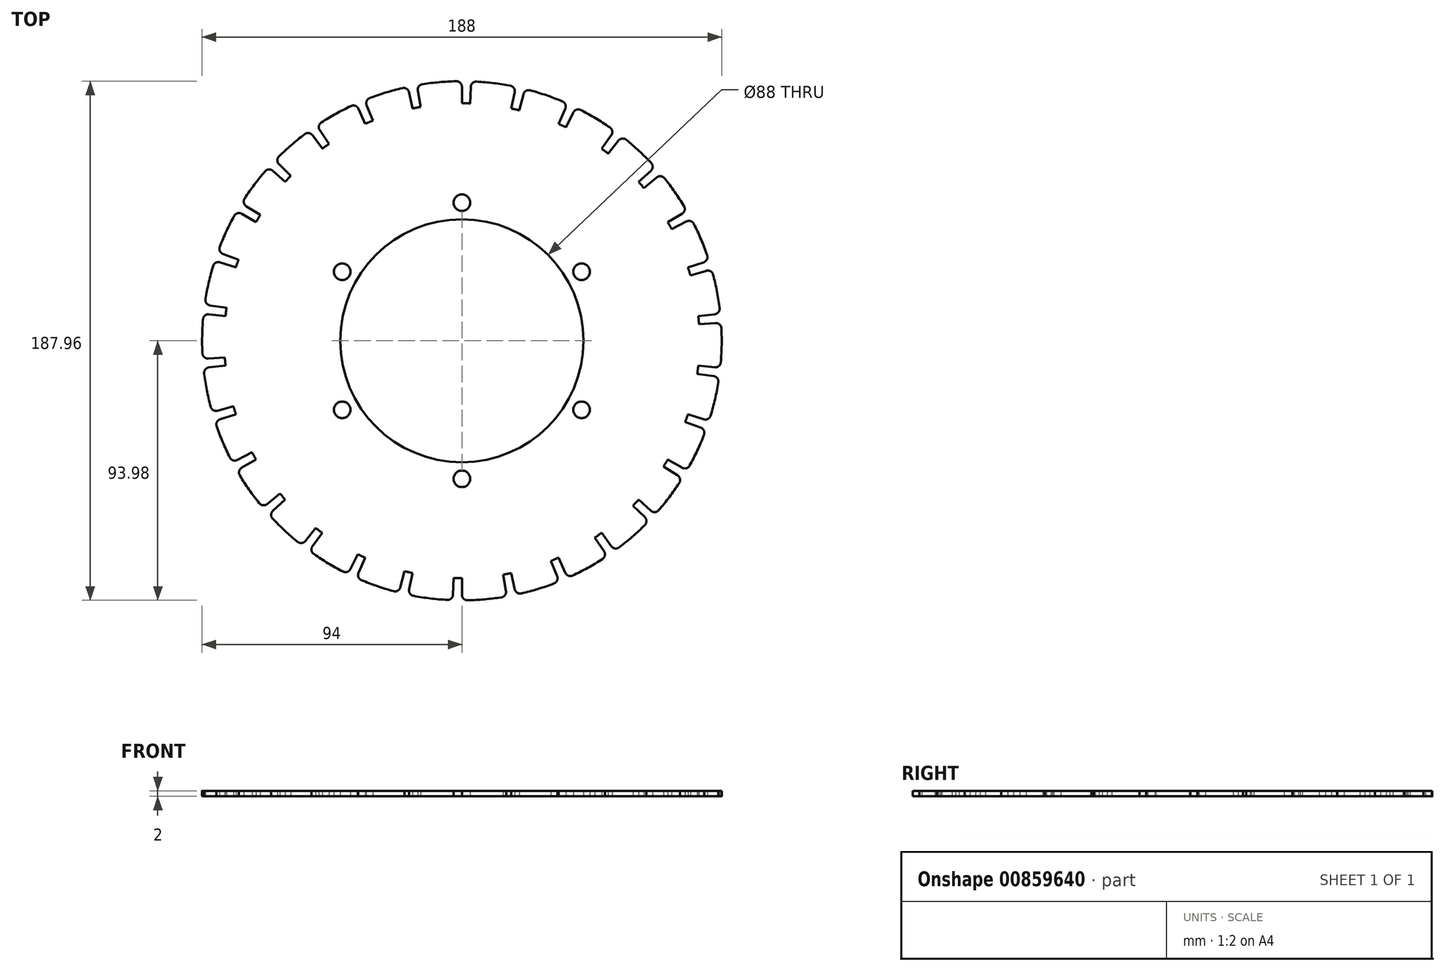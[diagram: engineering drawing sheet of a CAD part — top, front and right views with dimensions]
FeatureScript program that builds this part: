
annotation { "Feature Type Name" : "Feature", "Feature Type Description" : "" }
export const myFeature = defineFeature(function(context is Context, id is Id, definition is map)
    precondition{}
    {
        {
            var Q0;
            Q0=qCreatedBy(makeId("Top.planeOp"),FACE);
            var sketch = newSketch(context, id + "F0", { "sketchPlane" : qUnion([Q0])});
            skCircle(sketch, "E0", {"center": v(0, 0) * mm, "radius": 94 * mm});
            skCircle(sketch, "E1", {"center": v(0, 0) * mm, "radius": 44 * mm});
            skCircle(sketch, "E2", {"center": v(0, 50) * mm, "radius": 3 * mm});
            skCircle(sketch, "E3.1.0", {"center": v(-43.3, 25) * mm, "radius": 3 * mm});
            skCircle(sketch, "E3.2.0", {"center": v(-43.3, -25) * mm, "radius": 3 * mm});
            skCircle(sketch, "E3.3.0", {"center": v(0, -50) * mm, "radius": 3 * mm});
            skCircle(sketch, "E3.4.0", {"center": v(43.3, -25) * mm, "radius": 3 * mm});
            skCircle(sketch, "E3.5.0", {"center": v(43.3, 25) * mm, "radius": 3 * mm});
            skArc(sketch, "E4", {"start": v(0, 86) * mm, "mid": v(1.5, 85.99) * mm, "end": v(3, 85.95) * mm});
            skLineSegment(sketch, "E5", {"start": v(0, 94) * mm, "end": v(0, 86) * mm});
            skLineSegment(sketch, "E6", {"start": v(3.28, 93.94) * mm, "end": v(3, 85.95) * mm});
            skLineSegment(sketch, "E7", {"start": v(0, 0) * mm, "end": v(0, 86) * mm, "construction": true});
            skLineSegment(sketch, "E8", {"start": v(0, 0) * mm, "end": v(3, 85.95) * mm, "construction": true});
            skLineSegment(sketch, "E9.1.0", {"start": v(-16.32, 92.57) * mm, "end": v(-14.93, 84.7) * mm});
            skArc(sketch, "E9.1.1", {"start": v(-17.88, 84.12) * mm, "mid": v(-16.4, 84.42) * mm, "end": v(-14.93, 84.7) * mm});
            skLineSegment(sketch, "E9.1.2", {"start": v(-19.54, 91.95) * mm, "end": v(-17.88, 84.12) * mm});
            skLineSegment(sketch, "E9.2.0", {"start": v(-35.21, 87.16) * mm, "end": v(-32.22, 79.74) * mm});
            skArc(sketch, "E9.2.1", {"start": v(-34.98, 78.56) * mm, "mid": v(-33.6, 79.16) * mm, "end": v(-32.22, 79.74) * mm});
            skLineSegment(sketch, "E9.2.2", {"start": v(-38.23, 85.87) * mm, "end": v(-34.98, 78.56) * mm});
            skLineSegment(sketch, "E9.3.0", {"start": v(-52.56, 77.93) * mm, "end": v(-48.1, 71.3) * mm});
            skArc(sketch, "E9.3.1", {"start": v(-50.55, 69.58) * mm, "mid": v(-49.33, 70.45) * mm, "end": v(-48.1, 71.3) * mm});
            skLineSegment(sketch, "E9.3.2", {"start": v(-55.25, 76.05) * mm, "end": v(-50.55, 69.58) * mm});
            skLineSegment(sketch, "E9.4.0", {"start": v(-67.62, 65.3) * mm, "end": v(-61.86, 59.74) * mm});
            skArc(sketch, "E9.4.1", {"start": v(-63.91, 57.55) * mm, "mid": v(-62.9, 58.65) * mm, "end": v(-61.86, 59.74) * mm});
            skLineSegment(sketch, "E9.4.2", {"start": v(-69.86, 62.9) * mm, "end": v(-63.91, 57.55) * mm});
            skLineSegment(sketch, "E9.5.0", {"start": v(-79.72, 49.81) * mm, "end": v(-72.93, 45.57) * mm});
            skArc(sketch, "E9.5.1", {"start": v(-74.48, 43) * mm, "mid": v(-73.72, 44.3) * mm, "end": v(-72.93, 45.57) * mm});
            skLineSegment(sketch, "E9.5.2", {"start": v(-81.4, 47) * mm, "end": v(-74.48, 43) * mm});
            skLineSegment(sketch, "E9.6.0", {"start": v(-88.33, 32.15) * mm, "end": v(-80.81, 29.41) * mm});
            skArc(sketch, "E9.6.1", {"start": v(-81.8, 26.58) * mm, "mid": v(-81.31, 28) * mm, "end": v(-80.81, 29.41) * mm});
            skLineSegment(sketch, "E9.6.2", {"start": v(-89.4, 29.05) * mm, "end": v(-81.8, 26.58) * mm});
            skLineSegment(sketch, "E9.7.0", {"start": v(-93.09, 13.08) * mm, "end": v(-85.16, 11.97) * mm});
            skArc(sketch, "E9.7.1", {"start": v(-85.53, 8.99) * mm, "mid": v(-85.36, 10.48) * mm, "end": v(-85.16, 11.97) * mm});
            skLineSegment(sketch, "E9.7.2", {"start": v(-93.49, 9.83) * mm, "end": v(-85.53, 8.99) * mm});
            skLineSegment(sketch, "E9.8.0", {"start": v(-93.77, -6.56) * mm, "end": v(-85.8, -6) * mm});
            skArc(sketch, "E9.8.1", {"start": v(-85.53, -8.99) * mm, "mid": v(-85.67, -7.5) * mm, "end": v(-85.8, -6) * mm});
            skLineSegment(sketch, "E9.8.2", {"start": v(-93.49, -9.83) * mm, "end": v(-85.53, -8.99) * mm});
            skLineSegment(sketch, "E9.9.0", {"start": v(-90.36, -25.9) * mm, "end": v(-82.67, -23.7) * mm});
            skArc(sketch, "E9.9.1", {"start": v(-81.8, -26.58) * mm, "mid": v(-82.24, -25.14) * mm, "end": v(-82.67, -23.7) * mm});
            skLineSegment(sketch, "E9.9.2", {"start": v(-89.4, -29.05) * mm, "end": v(-81.8, -26.58) * mm});
            skLineSegment(sketch, "E9.10.0", {"start": v(-83, -44.13) * mm, "end": v(-75.93, -40.37) * mm});
            skArc(sketch, "E9.10.1", {"start": v(-74.48, -43) * mm, "mid": v(-75.22, -41.7) * mm, "end": v(-75.93, -40.37) * mm});
            skLineSegment(sketch, "E9.10.2", {"start": v(-81.4, -47) * mm, "end": v(-74.48, -43) * mm});
            skLineSegment(sketch, "E9.11.0", {"start": v(-72, -60.42) * mm, "end": v(-65.88, -55.28) * mm});
            skArc(sketch, "E9.11.1", {"start": v(-63.91, -57.55) * mm, "mid": v(-64.9, -56.42) * mm, "end": v(-65.88, -55.28) * mm});
            skLineSegment(sketch, "E9.11.2", {"start": v(-69.86, -62.9) * mm, "end": v(-63.91, -57.55) * mm});
            skLineSegment(sketch, "E9.12.0", {"start": v(-57.87, -74.07) * mm, "end": v(-52.95, -67.77) * mm});
            skArc(sketch, "E9.12.1", {"start": v(-50.55, -69.58) * mm, "mid": v(-51.76, -68.68) * mm, "end": v(-52.95, -67.77) * mm});
            skLineSegment(sketch, "E9.12.2", {"start": v(-55.25, -76.05) * mm, "end": v(-50.55, -69.58) * mm});
            skLineSegment(sketch, "E9.13.0", {"start": v(-41.2, -84.49) * mm, "end": v(-37.7, -77.3) * mm});
            skArc(sketch, "E9.13.1", {"start": v(-34.98, -78.56) * mm, "mid": v(-36.35, -77.94) * mm, "end": v(-37.7, -77.3) * mm});
            skLineSegment(sketch, "E9.13.2", {"start": v(-38.23, -85.87) * mm, "end": v(-34.98, -78.56) * mm});
            skLineSegment(sketch, "E9.14.0", {"start": v(-20.8, -83.45) * mm, "end": v(-22.74, -91.2) * mm});
            skArc(sketch, "E9.14.1", {"start": v(-17.88, -84.12) * mm, "mid": v(-19.35, -83.8) * mm, "end": v(-20.8, -83.45) * mm});
            skLineSegment(sketch, "E9.14.2", {"start": v(-19.54, -91.95) * mm, "end": v(-17.88, -84.12) * mm});
            skLineSegment(sketch, "E9.15.0", {"start": v(-3.28, -93.94) * mm, "end": v(-3, -85.95) * mm});
            skArc(sketch, "E9.15.1", {"start": v(0, -86) * mm, "mid": v(-1.5, -85.99) * mm, "end": v(-3, -85.95) * mm});
            skLineSegment(sketch, "E9.15.2", {"start": v(0, -94) * mm, "end": v(0, -86) * mm});
            skLineSegment(sketch, "E9.16.0", {"start": v(16.32, -92.57) * mm, "end": v(14.93, -84.7) * mm});
            skArc(sketch, "E9.16.1", {"start": v(17.88, -84.12) * mm, "mid": v(16.4, -84.42) * mm, "end": v(14.93, -84.7) * mm});
            skLineSegment(sketch, "E9.16.2", {"start": v(19.54, -91.95) * mm, "end": v(17.88, -84.12) * mm});
            skLineSegment(sketch, "E9.17.0", {"start": v(35.21, -87.16) * mm, "end": v(32.22, -79.74) * mm});
            skArc(sketch, "E9.17.1", {"start": v(34.98, -78.56) * mm, "mid": v(33.6, -79.16) * mm, "end": v(32.22, -79.74) * mm});
            skLineSegment(sketch, "E9.17.2", {"start": v(38.23, -85.87) * mm, "end": v(34.98, -78.56) * mm});
            skLineSegment(sketch, "E9.18.0", {"start": v(52.56, -77.93) * mm, "end": v(48.1, -71.3) * mm});
            skArc(sketch, "E9.18.1", {"start": v(50.55, -69.58) * mm, "mid": v(49.33, -70.45) * mm, "end": v(48.1, -71.3) * mm});
            skLineSegment(sketch, "E9.18.2", {"start": v(55.25, -76.05) * mm, "end": v(50.55, -69.58) * mm});
            skLineSegment(sketch, "E9.19.0", {"start": v(67.62, -65.3) * mm, "end": v(61.86, -59.74) * mm});
            skArc(sketch, "E9.19.1", {"start": v(63.91, -57.55) * mm, "mid": v(62.9, -58.65) * mm, "end": v(61.86, -59.74) * mm});
            skLineSegment(sketch, "E9.19.2", {"start": v(69.86, -62.9) * mm, "end": v(63.91, -57.55) * mm});
            skLineSegment(sketch, "E9.20.0", {"start": v(79.72, -49.81) * mm, "end": v(72.93, -45.57) * mm});
            skArc(sketch, "E9.20.1", {"start": v(74.48, -43) * mm, "mid": v(73.72, -44.3) * mm, "end": v(72.93, -45.57) * mm});
            skLineSegment(sketch, "E9.20.2", {"start": v(81.4, -47) * mm, "end": v(74.48, -43) * mm});
            skLineSegment(sketch, "E9.21.0", {"start": v(88.33, -32.15) * mm, "end": v(80.81, -29.41) * mm});
            skArc(sketch, "E9.21.1", {"start": v(81.8, -26.58) * mm, "mid": v(81.31, -28) * mm, "end": v(80.81, -29.41) * mm});
            skLineSegment(sketch, "E9.21.2", {"start": v(89.4, -29.05) * mm, "end": v(81.8, -26.58) * mm});
            skLineSegment(sketch, "E9.22.0", {"start": v(93.09, -13.08) * mm, "end": v(85.16, -11.97) * mm});
            skArc(sketch, "E9.22.1", {"start": v(85.53, -8.99) * mm, "mid": v(85.36, -10.48) * mm, "end": v(85.16, -11.97) * mm});
            skLineSegment(sketch, "E9.22.2", {"start": v(93.49, -9.83) * mm, "end": v(85.53, -8.99) * mm});
            skLineSegment(sketch, "E9.23.0", {"start": v(93.77, 6.56) * mm, "end": v(85.8, 6) * mm});
            skArc(sketch, "E9.23.1", {"start": v(85.53, 8.99) * mm, "mid": v(85.67, 7.5) * mm, "end": v(85.8, 6) * mm});
            skLineSegment(sketch, "E9.23.2", {"start": v(93.49, 9.83) * mm, "end": v(85.53, 8.99) * mm});
            skLineSegment(sketch, "E9.24.0", {"start": v(90.36, 25.9) * mm, "end": v(82.67, 23.7) * mm});
            skArc(sketch, "E9.24.1", {"start": v(81.8, 26.58) * mm, "mid": v(82.24, 25.14) * mm, "end": v(82.67, 23.7) * mm});
            skLineSegment(sketch, "E9.24.2", {"start": v(89.4, 29.05) * mm, "end": v(81.8, 26.58) * mm});
            skLineSegment(sketch, "E9.25.0", {"start": v(83, 44.13) * mm, "end": v(75.93, 40.37) * mm});
            skArc(sketch, "E9.25.1", {"start": v(74.48, 43) * mm, "mid": v(75.22, 41.7) * mm, "end": v(75.93, 40.37) * mm});
            skLineSegment(sketch, "E9.25.2", {"start": v(81.4, 47) * mm, "end": v(74.48, 43) * mm});
            skLineSegment(sketch, "E9.26.0", {"start": v(72, 60.42) * mm, "end": v(65.88, 55.28) * mm});
            skArc(sketch, "E9.26.1", {"start": v(63.91, 57.55) * mm, "mid": v(64.9, 56.42) * mm, "end": v(65.88, 55.28) * mm});
            skLineSegment(sketch, "E9.26.2", {"start": v(69.86, 62.9) * mm, "end": v(63.91, 57.55) * mm});
            skLineSegment(sketch, "E9.27.0", {"start": v(57.87, 74.07) * mm, "end": v(52.95, 67.77) * mm});
            skArc(sketch, "E9.27.1", {"start": v(50.55, 69.58) * mm, "mid": v(51.76, 68.68) * mm, "end": v(52.95, 67.77) * mm});
            skLineSegment(sketch, "E9.27.2", {"start": v(55.25, 76.05) * mm, "end": v(50.55, 69.58) * mm});
            skLineSegment(sketch, "E9.28.0", {"start": v(41.2, 84.49) * mm, "end": v(37.7, 77.3) * mm});
            skArc(sketch, "E9.28.1", {"start": v(34.98, 78.56) * mm, "mid": v(36.35, 77.94) * mm, "end": v(37.7, 77.3) * mm});
            skLineSegment(sketch, "E9.28.2", {"start": v(38.23, 85.87) * mm, "end": v(34.98, 78.56) * mm});
            skLineSegment(sketch, "E9.29.0", {"start": v(20.8, 83.45) * mm, "end": v(22.74, 91.2) * mm});
            skArc(sketch, "E9.29.1", {"start": v(17.88, 84.12) * mm, "mid": v(19.35, 83.8) * mm, "end": v(20.8, 83.45) * mm});
            skLineSegment(sketch, "E9.29.2", {"start": v(19.54, 91.95) * mm, "end": v(17.88, 84.12) * mm});
            skSolve(sketch);
        }
        {
            var Q0;
            Q0=makeQuery(id+"F0.imprint","IMPRINT",FACE,{"disambiguationData":[TD([[makeQuery(id+"F0.imprint","IMPRINT",EDGE,{"derivedFrom":sQuery(id+"F0.wireOp",EDGE,"E0")}),1.0]])]});
            extrude(context, id + "F1", {"entities" : qUnion([Q0]), "depth" : 2 * mm, "offsetDistance" : 25 * mm});
        }
        {
            var Q0;
            Q0=makeQuery(id+"F1.opExtrude","SWEPT_EDGE",EDGE,{"disambiguationData":[OSD([sQuery(id+"F0.wireOp",EDGE,"E0"),sQuery(id+"F0.wireOp",EDGE,"E9.4.0")])]});
            var Q1;
            Q1=makeQuery(id+"F1.opExtrude","SWEPT_EDGE",EDGE,{"disambiguationData":[OSD([sQuery(id+"F0.wireOp",EDGE,"E0"),sQuery(id+"F0.wireOp",EDGE,"E9.3.2")])]});
            var Q2;
            Q2=makeQuery(id+"F1.opExtrude","SWEPT_EDGE",EDGE,{"disambiguationData":[OSD([sQuery(id+"F0.wireOp",EDGE,"E0"),sQuery(id+"F0.wireOp",EDGE,"E9.3.0")])]});
            var Q3;
            Q3=makeQuery(id+"F1.opExtrude","SWEPT_EDGE",EDGE,{"disambiguationData":[OSD([sQuery(id+"F0.wireOp",EDGE,"E0"),sQuery(id+"F0.wireOp",EDGE,"E9.2.2")])]});
            var Q4;
            Q4=makeQuery(id+"F1.opExtrude","SWEPT_EDGE",EDGE,{"disambiguationData":[OSD([sQuery(id+"F0.wireOp",EDGE,"E0"),sQuery(id+"F0.wireOp",EDGE,"E9.2.0")])]});
            var Q5;
            Q5=makeQuery(id+"F1.opExtrude","SWEPT_EDGE",EDGE,{"disambiguationData":[OSD([sQuery(id+"F0.wireOp",EDGE,"E0"),sQuery(id+"F0.wireOp",EDGE,"E9.1.2")])]});
            var Q6;
            Q6=makeQuery(id+"F1.opExtrude","SWEPT_EDGE",EDGE,{"disambiguationData":[OSD([sQuery(id+"F0.wireOp",EDGE,"E0"),sQuery(id+"F0.wireOp",EDGE,"E9.1.0")])]});
            var Q7;
            Q7=makeQuery(id+"F1.opExtrude","SWEPT_EDGE",EDGE,{"disambiguationData":[OSD([sQuery(id+"F0.wireOp",EDGE,"E0"),sQuery(id+"F0.wireOp",EDGE,"E5")])]});
            var Q8;
            Q8=makeQuery(id+"F1.opExtrude","SWEPT_EDGE",EDGE,{"disambiguationData":[OSD([sQuery(id+"F0.wireOp",EDGE,"E0"),sQuery(id+"F0.wireOp",EDGE,"E6")])]});
            var Q9;
            Q9=makeQuery(id+"F1.opExtrude","SWEPT_EDGE",EDGE,{"disambiguationData":[OSD([sQuery(id+"F0.wireOp",EDGE,"E0"),sQuery(id+"F0.wireOp",EDGE,"E9.29.2")])]});
            var Q10;
            Q10=makeQuery(id+"F1.opExtrude","SWEPT_EDGE",EDGE,{"disambiguationData":[OSD([sQuery(id+"F0.wireOp",EDGE,"E0"),sQuery(id+"F0.wireOp",EDGE,"E9.29.0")])]});
            var Q11;
            Q11=makeQuery(id+"F1.opExtrude","SWEPT_EDGE",EDGE,{"disambiguationData":[OSD([sQuery(id+"F0.wireOp",EDGE,"E0"),sQuery(id+"F0.wireOp",EDGE,"E9.28.2")])]});
            var Q12;
            Q12=makeQuery(id+"F1.opExtrude","SWEPT_EDGE",EDGE,{"disambiguationData":[OSD([sQuery(id+"F0.wireOp",EDGE,"E0"),sQuery(id+"F0.wireOp",EDGE,"E9.28.0")])]});
            var Q13;
            Q13=makeQuery(id+"F1.opExtrude","SWEPT_EDGE",EDGE,{"disambiguationData":[OSD([sQuery(id+"F0.wireOp",EDGE,"E0"),sQuery(id+"F0.wireOp",EDGE,"E9.27.2")])]});
            var Q14;
            Q14=makeQuery(id+"F1.opExtrude","SWEPT_EDGE",EDGE,{"disambiguationData":[OSD([sQuery(id+"F0.wireOp",EDGE,"E0"),sQuery(id+"F0.wireOp",EDGE,"E9.27.0")])]});
            var Q15;
            Q15=makeQuery(id+"F1.opExtrude","SWEPT_EDGE",EDGE,{"disambiguationData":[OSD([sQuery(id+"F0.wireOp",EDGE,"E0"),sQuery(id+"F0.wireOp",EDGE,"E9.26.2")])]});
            var Q16;
            Q16=makeQuery(id+"F1.opExtrude","SWEPT_EDGE",EDGE,{"disambiguationData":[OSD([sQuery(id+"F0.wireOp",EDGE,"E0"),sQuery(id+"F0.wireOp",EDGE,"E9.26.0")])]});
            var Q17;
            Q17=makeQuery(id+"F1.opExtrude","SWEPT_EDGE",EDGE,{"disambiguationData":[OSD([sQuery(id+"F0.wireOp",EDGE,"E0"),sQuery(id+"F0.wireOp",EDGE,"E9.25.2")])]});
            var Q18;
            Q18=makeQuery(id+"F1.opExtrude","SWEPT_EDGE",EDGE,{"disambiguationData":[OSD([sQuery(id+"F0.wireOp",EDGE,"E0"),sQuery(id+"F0.wireOp",EDGE,"E9.25.0")])]});
            var Q19;
            Q19=makeQuery(id+"F1.opExtrude","SWEPT_EDGE",EDGE,{"disambiguationData":[OSD([sQuery(id+"F0.wireOp",EDGE,"E0"),sQuery(id+"F0.wireOp",EDGE,"E9.24.2")])]});
            var Q20;
            Q20=makeQuery(id+"F1.opExtrude","SWEPT_EDGE",EDGE,{"disambiguationData":[OSD([sQuery(id+"F0.wireOp",EDGE,"E0"),sQuery(id+"F0.wireOp",EDGE,"E9.24.0")])]});
            var Q21;
            Q21=makeQuery(id+"F1.opExtrude","SWEPT_EDGE",EDGE,{"disambiguationData":[OSD([sQuery(id+"F0.wireOp",EDGE,"E0"),sQuery(id+"F0.wireOp",EDGE,"E9.23.2")])]});
            var Q22;
            Q22=makeQuery(id+"F1.opExtrude","SWEPT_EDGE",EDGE,{"disambiguationData":[OSD([sQuery(id+"F0.wireOp",EDGE,"E0"),sQuery(id+"F0.wireOp",EDGE,"E9.23.0")])]});
            var Q23;
            Q23=makeQuery(id+"F1.opExtrude","SWEPT_EDGE",EDGE,{"disambiguationData":[OSD([sQuery(id+"F0.wireOp",EDGE,"E0"),sQuery(id+"F0.wireOp",EDGE,"E9.22.2")])]});
            var Q24;
            Q24=makeQuery(id+"F1.opExtrude","SWEPT_EDGE",EDGE,{"disambiguationData":[OSD([sQuery(id+"F0.wireOp",EDGE,"E0"),sQuery(id+"F0.wireOp",EDGE,"E9.22.0")])]});
            var Q25;
            Q25=makeQuery(id+"F1.opExtrude","SWEPT_EDGE",EDGE,{"disambiguationData":[OSD([sQuery(id+"F0.wireOp",EDGE,"E0"),sQuery(id+"F0.wireOp",EDGE,"E9.21.2")])]});
            var Q26;
            Q26=makeQuery(id+"F1.opExtrude","SWEPT_EDGE",EDGE,{"disambiguationData":[OSD([sQuery(id+"F0.wireOp",EDGE,"E0"),sQuery(id+"F0.wireOp",EDGE,"E9.21.0")])]});
            var Q27;
            Q27=makeQuery(id+"F1.opExtrude","SWEPT_EDGE",EDGE,{"disambiguationData":[OSD([sQuery(id+"F0.wireOp",EDGE,"E0"),sQuery(id+"F0.wireOp",EDGE,"E9.20.2")])]});
            var Q28;
            Q28=makeQuery(id+"F1.opExtrude","SWEPT_EDGE",EDGE,{"disambiguationData":[OSD([sQuery(id+"F0.wireOp",EDGE,"E0"),sQuery(id+"F0.wireOp",EDGE,"E9.20.0")])]});
            var Q29;
            Q29=makeQuery(id+"F1.opExtrude","SWEPT_EDGE",EDGE,{"disambiguationData":[OSD([sQuery(id+"F0.wireOp",EDGE,"E0"),sQuery(id+"F0.wireOp",EDGE,"E9.19.2")])]});
            var Q30;
            Q30=makeQuery(id+"F1.opExtrude","SWEPT_EDGE",EDGE,{"disambiguationData":[OSD([sQuery(id+"F0.wireOp",EDGE,"E0"),sQuery(id+"F0.wireOp",EDGE,"E9.19.0")])]});
            var Q31;
            Q31=makeQuery(id+"F1.opExtrude","SWEPT_EDGE",EDGE,{"disambiguationData":[OSD([sQuery(id+"F0.wireOp",EDGE,"E0"),sQuery(id+"F0.wireOp",EDGE,"E9.18.2")])]});
            var Q32;
            Q32=makeQuery(id+"F1.opExtrude","SWEPT_EDGE",EDGE,{"disambiguationData":[OSD([sQuery(id+"F0.wireOp",EDGE,"E0"),sQuery(id+"F0.wireOp",EDGE,"E9.18.0")])]});
            var Q33;
            Q33=makeQuery(id+"F1.opExtrude","SWEPT_EDGE",EDGE,{"disambiguationData":[OSD([sQuery(id+"F0.wireOp",EDGE,"E0"),sQuery(id+"F0.wireOp",EDGE,"E9.17.2")])]});
            var Q34;
            Q34=makeQuery(id+"F1.opExtrude","SWEPT_EDGE",EDGE,{"disambiguationData":[OSD([sQuery(id+"F0.wireOp",EDGE,"E0"),sQuery(id+"F0.wireOp",EDGE,"E9.17.0")])]});
            var Q35;
            Q35=makeQuery(id+"F1.opExtrude","SWEPT_EDGE",EDGE,{"disambiguationData":[OSD([sQuery(id+"F0.wireOp",EDGE,"E0"),sQuery(id+"F0.wireOp",EDGE,"E9.16.2")])]});
            var Q36;
            Q36=makeQuery(id+"F1.opExtrude","SWEPT_EDGE",EDGE,{"disambiguationData":[OSD([sQuery(id+"F0.wireOp",EDGE,"E0"),sQuery(id+"F0.wireOp",EDGE,"E9.16.0")])]});
            var Q37;
            Q37=makeQuery(id+"F1.opExtrude","SWEPT_EDGE",EDGE,{"disambiguationData":[OSD([sQuery(id+"F0.wireOp",EDGE,"E0"),sQuery(id+"F0.wireOp",EDGE,"E9.15.2")])]});
            var Q38;
            Q38=makeQuery(id+"F1.opExtrude","SWEPT_EDGE",EDGE,{"disambiguationData":[OSD([sQuery(id+"F0.wireOp",EDGE,"E0"),sQuery(id+"F0.wireOp",EDGE,"E9.15.0")])]});
            var Q39;
            Q39=makeQuery(id+"F1.opExtrude","SWEPT_EDGE",EDGE,{"disambiguationData":[OSD([sQuery(id+"F0.wireOp",EDGE,"E0"),sQuery(id+"F0.wireOp",EDGE,"E9.14.2")])]});
            var Q40;
            Q40=makeQuery(id+"F1.opExtrude","SWEPT_EDGE",EDGE,{"disambiguationData":[OSD([sQuery(id+"F0.wireOp",EDGE,"E0"),sQuery(id+"F0.wireOp",EDGE,"E9.14.0")])]});
            var Q41;
            Q41=makeQuery(id+"F1.opExtrude","SWEPT_EDGE",EDGE,{"disambiguationData":[OSD([sQuery(id+"F0.wireOp",EDGE,"E0"),sQuery(id+"F0.wireOp",EDGE,"E9.13.2")])]});
            var Q42;
            Q42=makeQuery(id+"F1.opExtrude","SWEPT_EDGE",EDGE,{"disambiguationData":[OSD([sQuery(id+"F0.wireOp",EDGE,"E0"),sQuery(id+"F0.wireOp",EDGE,"E9.13.0")])]});
            var Q43;
            Q43=makeQuery(id+"F1.opExtrude","SWEPT_EDGE",EDGE,{"disambiguationData":[OSD([sQuery(id+"F0.wireOp",EDGE,"E0"),sQuery(id+"F0.wireOp",EDGE,"E9.12.2")])]});
            var Q44;
            Q44=makeQuery(id+"F1.opExtrude","SWEPT_EDGE",EDGE,{"disambiguationData":[OSD([sQuery(id+"F0.wireOp",EDGE,"E0"),sQuery(id+"F0.wireOp",EDGE,"E9.12.0")])]});
            var Q45;
            Q45=makeQuery(id+"F1.opExtrude","SWEPT_EDGE",EDGE,{"disambiguationData":[OSD([sQuery(id+"F0.wireOp",EDGE,"E0"),sQuery(id+"F0.wireOp",EDGE,"E9.11.2")])]});
            var Q46;
            Q46=makeQuery(id+"F1.opExtrude","SWEPT_EDGE",EDGE,{"disambiguationData":[OSD([sQuery(id+"F0.wireOp",EDGE,"E0"),sQuery(id+"F0.wireOp",EDGE,"E9.11.0")])]});
            var Q47;
            Q47=makeQuery(id+"F1.opExtrude","SWEPT_EDGE",EDGE,{"disambiguationData":[OSD([sQuery(id+"F0.wireOp",EDGE,"E0"),sQuery(id+"F0.wireOp",EDGE,"E9.10.2")])]});
            var Q48;
            Q48=makeQuery(id+"F1.opExtrude","SWEPT_EDGE",EDGE,{"disambiguationData":[OSD([sQuery(id+"F0.wireOp",EDGE,"E0"),sQuery(id+"F0.wireOp",EDGE,"E9.10.0")])]});
            var Q49;
            Q49=makeQuery(id+"F1.opExtrude","SWEPT_EDGE",EDGE,{"disambiguationData":[OSD([sQuery(id+"F0.wireOp",EDGE,"E0"),sQuery(id+"F0.wireOp",EDGE,"E9.9.2")])]});
            var Q50;
            Q50=makeQuery(id+"F1.opExtrude","SWEPT_EDGE",EDGE,{"disambiguationData":[OSD([sQuery(id+"F0.wireOp",EDGE,"E0"),sQuery(id+"F0.wireOp",EDGE,"E9.9.0")])]});
            var Q51;
            Q51=makeQuery(id+"F1.opExtrude","SWEPT_EDGE",EDGE,{"disambiguationData":[OSD([sQuery(id+"F0.wireOp",EDGE,"E0"),sQuery(id+"F0.wireOp",EDGE,"E9.8.2")])]});
            var Q52;
            Q52=makeQuery(id+"F1.opExtrude","SWEPT_EDGE",EDGE,{"disambiguationData":[OSD([sQuery(id+"F0.wireOp",EDGE,"E0"),sQuery(id+"F0.wireOp",EDGE,"E9.8.0")])]});
            var Q53;
            Q53=makeQuery(id+"F1.opExtrude","SWEPT_EDGE",EDGE,{"disambiguationData":[OSD([sQuery(id+"F0.wireOp",EDGE,"E0"),sQuery(id+"F0.wireOp",EDGE,"E9.7.0")])]});
            var Q54;
            Q54=makeQuery(id+"F1.opExtrude","SWEPT_EDGE",EDGE,{"disambiguationData":[OSD([sQuery(id+"F0.wireOp",EDGE,"E0"),sQuery(id+"F0.wireOp",EDGE,"E9.7.2")])]});
            var Q55;
            Q55=makeQuery(id+"F1.opExtrude","SWEPT_EDGE",EDGE,{"disambiguationData":[OSD([sQuery(id+"F0.wireOp",EDGE,"E0"),sQuery(id+"F0.wireOp",EDGE,"E9.6.2")])]});
            var Q56;
            Q56=makeQuery(id+"F1.opExtrude","SWEPT_EDGE",EDGE,{"disambiguationData":[OSD([sQuery(id+"F0.wireOp",EDGE,"E0"),sQuery(id+"F0.wireOp",EDGE,"E9.6.0")])]});
            var Q57;
            Q57=makeQuery(id+"F1.opExtrude","SWEPT_EDGE",EDGE,{"disambiguationData":[OSD([sQuery(id+"F0.wireOp",EDGE,"E0"),sQuery(id+"F0.wireOp",EDGE,"E9.5.2")])]});
            var Q58;
            Q58=makeQuery(id+"F1.opExtrude","SWEPT_EDGE",EDGE,{"disambiguationData":[OSD([sQuery(id+"F0.wireOp",EDGE,"E0"),sQuery(id+"F0.wireOp",EDGE,"E9.5.0")])]});
            var Q59;
            Q59=makeQuery(id+"F1.opExtrude","SWEPT_EDGE",EDGE,{"disambiguationData":[OSD([sQuery(id+"F0.wireOp",EDGE,"E0"),sQuery(id+"F0.wireOp",EDGE,"E9.4.2")])]});
            fillet(context, id + "F2", {"entities" : qUnion([Q0, Q1, Q2, Q3, Q4, Q5, Q6, Q7, Q8, Q9, Q10, Q11, Q12, Q13, Q14, Q15, Q16, Q17, Q18, Q19, Q20, Q21, Q22, Q23, Q24, Q25, Q26, Q27, Q28, Q29, Q30, Q31, Q32, Q33, Q34, Q35, Q36, Q37, Q38, Q39, Q40, Q41, Q42, Q43, Q44, Q45, Q46, Q47, Q48, Q49, Q50, Q51, Q52, Q53, Q54, Q55, Q56, Q57, Q58, Q59]), "radius" : 2 * mm, "tangentPropagation" : true, "allowEdgeOverflow" : false});
        }
    });
